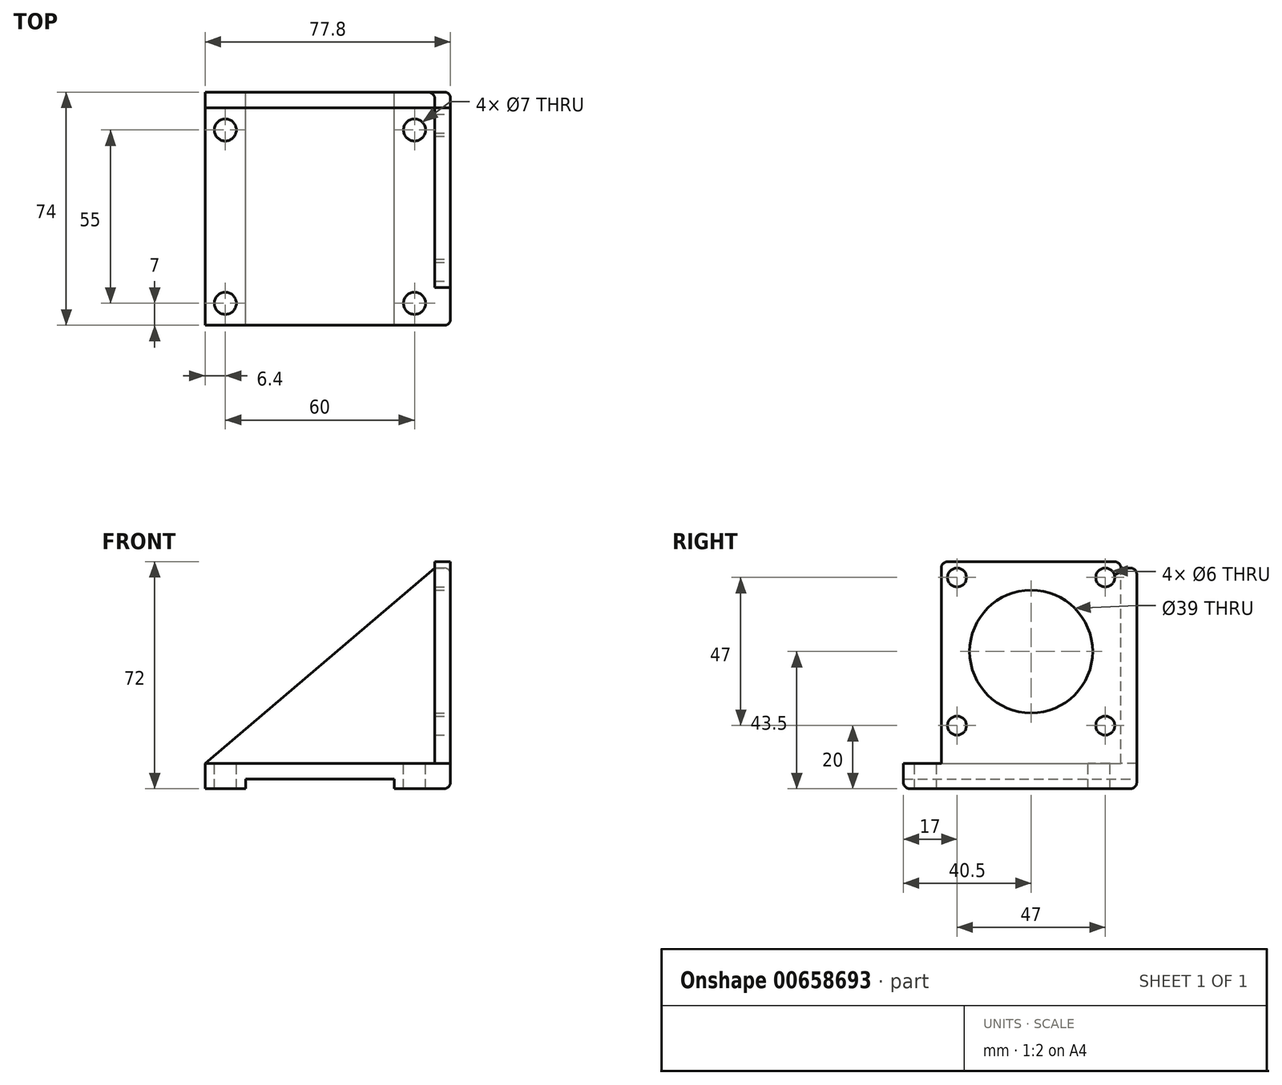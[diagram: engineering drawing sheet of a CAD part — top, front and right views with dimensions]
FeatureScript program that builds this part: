
annotation { "Feature Type Name" : "Feature", "Feature Type Description" : "" }
export const myFeature = defineFeature(function(context is Context, id is Id, definition is map)
    precondition{}
    {
        {
            var Q0;
            Q0=qCreatedBy(makeId("Top.planeOp"),FACE);
            var sketch = newSketch(context, id + "F0", { "sketchPlane" : qUnion([Q0])});
            skLineSegment(sketch, "E0.rect.bottom", {"start": v(36.4, -34.5) * mm, "end": v(-36.4, -34.5) * mm});
            skLineSegment(sketch, "E0.rect.top", {"start": v(36.4, 34.5) * mm, "end": v(-36.4, 34.5) * mm});
            skLineSegment(sketch, "E0.rect.left", {"start": v(36.4, -34.5) * mm, "end": v(36.4, 34.5) * mm});
            skLineSegment(sketch, "E0.rect.right", {"start": v(-36.4, -34.5) * mm, "end": v(-36.4, 34.5) * mm});
            skPoint(sketch, "E0.rect.middle", {"position": v(0, 0) * mm});
            skSolve(sketch);
        }
        {
            var Q0;
            Q0=makeQuery(id+"F0.imprint","IMPRINT",FACE,{"disambiguationData":[TD([[makeQuery(id+"F0.imprint","IMPRINT",EDGE,{"derivedFrom":sQuery(id+"F0.wireOp",EDGE,"E0.rect.bottom")}),-1.0]])]});
            extrude(context, id + "F1", {"entities" : qUnion([Q0]), "depth" : 5 * mm});
        }
        {
            var Q0;
            Q0=makeQuery(id+"F1.opExtrude","CAP_FACE",FACE,{"disambiguationData":[OSD([sQuery(id+"F0.wireOp",EDGE,"E0.rect.bottom"),sQuery(id+"F0.wireOp",EDGE,"E0.rect.top"),sQuery(id+"F0.wireOp",EDGE,"E0.rect.left"),sQuery(id+"F0.wireOp",EDGE,"E0.rect.right")])],"isStart":false});
            var sketch = newSketch(context, id + "F2", { "sketchPlane" : qUnion([Q0])});
            skPoint(sketch, "E1", {"position": v(-30, 27.5) * mm});
            skPoint(sketch, "E2", {"position": v(30, 27.5) * mm});
            skPoint(sketch, "E3", {"position": v(30, -27.5) * mm});
            skPoint(sketch, "E4", {"position": v(-30, -27.5) * mm});
            skLineSegment(sketch, "E5.0", {"start": v(36.4, 34.5) * mm, "end": v(-36.4, 34.5) * mm});
            skLineSegment(sketch, "E6.0", {"start": v(36.4, -34.5) * mm, "end": v(-36.4, -34.5) * mm});
            skSolve(sketch);
        }
        {
            var Q0;
            Q0=sQuery(id+"F2.wireOp",VERTEX,"E1");
            var Q1;
            Q1=sQuery(id+"F2.wireOp",VERTEX,"E2");
            var Q2;
            Q2=sQuery(id+"F2.wireOp",VERTEX,"E3");
            var Q3;
            Q3=sQuery(id+"F2.wireOp",VERTEX,"E4");
            var Q4;
            Q4=makeQuery(id+"F1.opExtrude","SWEPT_BODY",BODY,{"disambiguationData":[OSD([sQuery(id+"F0.wireOp",EDGE,"E0.rect.bottom"),sQuery(id+"F0.wireOp",EDGE,"E0.rect.top"),sQuery(id+"F0.wireOp",EDGE,"E0.rect.left"),sQuery(id+"F0.wireOp",EDGE,"E0.rect.right")])]});
            hole(context, id + "F3", {"style" : HoleStyle.SIMPLE, "holeDiameter" : 7 * mm, "endStyle" : HoleEndStyle.THROUGH, "locations" : qUnion([Q0, Q1, Q2, Q3]), "scope" : qUnion([Q4])});
        }
        {
            var Q0;
            Q0=makeQuery(id+"F1.opExtrude","CAP_FACE",FACE,{"disambiguationData":[OSD([sQuery(id+"F0.wireOp",EDGE,"E0.rect.bottom"),sQuery(id+"F0.wireOp",EDGE,"E0.rect.top"),sQuery(id+"F0.wireOp",EDGE,"E0.rect.left"),sQuery(id+"F0.wireOp",EDGE,"E0.rect.right")])],"isStart":true});
            var sketch = newSketch(context, id + "F4", { "sketchPlane" : qUnion([Q0])});
            skCircle(sketch, "E7.0", {"center": v(-30, 27.5) * mm, "radius": 3.5 * mm});
            skLineSegment(sketch, "E8.bottom", {"start": v(-36.4, 34.5) * mm, "end": v(-23.6, 34.5) * mm});
            skLineSegment(sketch, "E8.top", {"start": v(-36.4, -34.5) * mm, "end": v(-23.6, -34.5) * mm});
            skLineSegment(sketch, "E8.left", {"start": v(-36.4, 34.5) * mm, "end": v(-36.4, -34.5) * mm});
            skLineSegment(sketch, "E8.right", {"start": v(-23.6, 34.5) * mm, "end": v(-23.6, -34.5) * mm});
            skLineSegment(sketch, "E9.bottom", {"start": v(36.4, 34.5) * mm, "end": v(23.6, 34.5) * mm});
            skLineSegment(sketch, "E9.top", {"start": v(36.4, -34.5) * mm, "end": v(23.6, -34.5) * mm});
            skLineSegment(sketch, "E9.left", {"start": v(36.4, 34.5) * mm, "end": v(36.4, -34.5) * mm});
            skLineSegment(sketch, "E9.right", {"start": v(23.6, 34.5) * mm, "end": v(23.6, -34.5) * mm});
            skSolve(sketch);
        }
        {
            var Q0;
            Q0=makeQuery(id+"F4.imprint","IMPRINT",FACE,{"disambiguationData":[TD([[makeQuery(id+"F4.imprint","IMPRINT",EDGE,{"derivedFrom":sQuery(id+"F4.wireOp",EDGE,"E7.0")}),-1.0]])]});
            var Q1;
            Q1=makeQuery(id+"F4.imprint","IMPRINT",FACE,{"disambiguationData":[TD([[makeQuery(id+"F4.imprint","IMPRINT",EDGE,{"derivedFrom":sQuery(id+"F4.wireOp",EDGE,"E9.bottom")}),1.0]])]});
            extrude(context, id + "F5", {"entities" : qUnion([Q0, Q1]), "operationType" : NewBodyOperationType.ADD, "depth" : 3 * mm});
        }
        {
            var Q0;
            Q0=makeQuery(id+"F5.boolean.opBoolean","MERGE",FACE,{"derivedFrom":[makeQuery(id+"F1.opExtrude","SWEPT_FACE",FACE,{"disambiguationData":[OSD([sQuery(id+"F0.wireOp",EDGE,"E0.rect.left")])]}),makeQuery(id+"F5.opExtrude","SWEPT_FACE",FACE,{"disambiguationData":[OSD([sQuery(id+"F4.wireOp",EDGE,"E9.left")])]})]});
            var sketch = newSketch(context, id + "F6", { "sketchPlane" : qUnion([Q0])});
            skLineSegment(sketch, "E10.bottom", {"start": v(34.5, 5) * mm, "end": v(-22.5, 5) * mm});
            skLineSegment(sketch, "E10.top", {"start": v(34.5, 69) * mm, "end": v(-22.5, 69) * mm});
            skLineSegment(sketch, "E10.left", {"start": v(34.5, 5) * mm, "end": v(34.5, 69) * mm});
            skLineSegment(sketch, "E10.right", {"start": v(-22.5, 5) * mm, "end": v(-22.5, 69) * mm});
            skSolve(sketch);
        }
        {
            var Q0;
            Q0=makeQuery(id+"F6.imprint","IMPRINT",FACE,{"disambiguationData":[TD([[makeQuery(id+"F6.imprint","IMPRINT",EDGE,{"derivedFrom":sQuery(id+"F6.wireOp",EDGE,"E10.bottom")}),1.0]])]});
            var Q1;
            {var subQ4=sQuery(id+"F6.wireOp",EDGE,"E10.bottom");Q1=makeQuery(id+"F6.imprint","IMPRINT",FACE,{"disambiguationData":[TD([[makeQuery(id+"F6.imprint","IMPRINT",EDGE,{"derivedFrom":subQ4}),-1.0]])]});}
            extrude(context, id + "F7", {"entities" : qUnion([Q0, Q1]), "operationType" : NewBodyOperationType.ADD, "depth" : 5 * mm});
        }
        {
            var Q0;
            Q0=makeQuery(id+"F7.opExtrude","SWEPT_EDGE",EDGE,{"disambiguationData":[OSD([sQuery(id+"F6.wireOp",EDGE,"E10.top"),sQuery(id+"F6.wireOp",EDGE,"E10.left")])]});
            var Q1;
            Q1=makeQuery(id+"F7.opExtrude","SWEPT_EDGE",EDGE,{"disambiguationData":[OSD([sQuery(id+"F6.wireOp",EDGE,"E10.top"),sQuery(id+"F6.wireOp",EDGE,"E10.right")])]});
            fillet(context, id + "F8", {"entities" : qUnion([Q0, Q1]), "radius" : 2 * mm, "tangentPropagation" : true, "allowEdgeOverflow" : false});
        }
        {
            var Q0;
            Q0=makeQuery(id+"F7.opExtrude","CAP_FACE",FACE,{"disambiguationData":[OSD([sQuery(id+"F0.wireOp",EDGE,"E0.rect.bottom"),sQuery(id+"F0.wireOp",EDGE,"E0.rect.top"),sQuery(id+"F0.wireOp",EDGE,"E0.rect.left"),sQuery(id+"F4.wireOp",EDGE,"E9.bottom"),sQuery(id+"F4.wireOp",EDGE,"E9.top"),sQuery(id+"F4.wireOp",EDGE,"E9.left"),sQuery(id+"F6.wireOp",EDGE,"E10.top"),sQuery(id+"F6.wireOp",EDGE,"E10.left"),sQuery(id+"F6.wireOp",EDGE,"E10.right")])],"isStart":false});
            var sketch = newSketch(context, id + "F9", { "sketchPlane" : qUnion([Q0])});
            skLineSegment(sketch, "E11", {"start": v(6, 69) * mm, "end": v(6, 40.5) * mm, "construction": true});
            skCircle(sketch, "E12", {"center": v(6, 40.5) * mm, "radius": 19.5 * mm});
            skSolve(sketch);
        }
        {
            var Q0;
            Q0=makeQuery(id+"F9.imprint","IMPRINT",FACE,{"disambiguationData":[TD([[makeQuery(id+"F9.imprint","IMPRINT",EDGE,{"derivedFrom":sQuery(id+"F9.wireOp",EDGE,"E12")}),1.0]])]});
            extrude(context, id + "F10", {"entities" : qUnion([Q0]), "operationType" : NewBodyOperationType.REMOVE, "endBound" : BoundingType.THROUGH_ALL, "oppositeDirection" : true, "depth" : 25 * mm});
        }
        {
            var Q0;
            Q0=makeQuery(id+"F7.opExtrude","CAP_FACE",FACE,{"disambiguationData":[OSD([sQuery(id+"F0.wireOp",EDGE,"E0.rect.bottom"),sQuery(id+"F0.wireOp",EDGE,"E0.rect.top"),sQuery(id+"F0.wireOp",EDGE,"E0.rect.left"),sQuery(id+"F4.wireOp",EDGE,"E9.bottom"),sQuery(id+"F4.wireOp",EDGE,"E9.top"),sQuery(id+"F4.wireOp",EDGE,"E9.left"),sQuery(id+"F6.wireOp",EDGE,"E10.top"),sQuery(id+"F6.wireOp",EDGE,"E10.left"),sQuery(id+"F6.wireOp",EDGE,"E10.right")])],"isStart":false});
            var sketch = newSketch(context, id + "F11", { "sketchPlane" : qUnion([Q0])});
            skPoint(sketch, "E13", {"position": v(-17.5, 64) * mm});
            skPoint(sketch, "E14", {"position": v(29.5, 64) * mm});
            skPoint(sketch, "E15", {"position": v(29.5, 17) * mm});
            skPoint(sketch, "E16", {"position": v(-17.5, 17) * mm});
            skCircle(sketch, "E17.0", {"center": v(6, 40.5) * mm, "radius": 19.5 * mm});
            skSolve(sketch);
        }
        {
            var Q0;
            Q0=sQuery(id+"F11.wireOp",VERTEX,"E13");
            var Q1;
            Q1=sQuery(id+"F11.wireOp",VERTEX,"E14");
            var Q2;
            Q2=sQuery(id+"F11.wireOp",VERTEX,"E15");
            var Q3;
            Q3=sQuery(id+"F11.wireOp",VERTEX,"E16");
            var Q4;
            Q4=makeQuery(id+"F1.opExtrude","SWEPT_BODY",BODY,{"disambiguationData":[OSD([sQuery(id+"F0.wireOp",EDGE,"E0.rect.bottom"),sQuery(id+"F0.wireOp",EDGE,"E0.rect.top"),sQuery(id+"F0.wireOp",EDGE,"E0.rect.left"),sQuery(id+"F0.wireOp",EDGE,"E0.rect.right")])]});
            hole(context, id + "F12", {"style" : HoleStyle.SIMPLE, "holeDiameter" : 6 * mm, "endStyle" : HoleEndStyle.THROUGH, "locations" : qUnion([Q0, Q1, Q2, Q3]), "scope" : qUnion([Q4])});
        }
        {
            var Q0;
            {var subQ0=sQuery(id+"F4.wireOp",EDGE,"E9.top");var subQ1=sQuery(id+"F0.wireOp",EDGE,"E0.rect.top");Q0=makeQuery(id+"F7.boolean.opBoolean","MERGE",FACE,{"derivedFrom":[makeQuery(id+"F5.boolean.opBoolean","MERGE",FACE,{"derivedFrom":[makeQuery(id+"F1.opExtrude","SWEPT_FACE",FACE,{"disambiguationData":[OSD([subQ1])]}),makeQuery(id+"F5.opExtrude","SWEPT_FACE",FACE,{"disambiguationData":[OSD([sQuery(id+"F4.wireOp",EDGE,"E8.top")])]}),makeQuery(id+"F5.opExtrude","SWEPT_FACE",FACE,{"disambiguationData":[OSD([subQ0])]})]}),makeQuery(id+"F7.opExtrude","SWEPT_FACE",FACE,{"disambiguationData":[OSD([subQ1,sQuery(id+"F0.wireOp",EDGE,"E0.rect.left"),subQ0,sQuery(id+"F4.wireOp",EDGE,"E9.left"),sQuery(id+"F6.wireOp",EDGE,"E10.left")])]})]});}
            var sketch = newSketch(context, id + "F13", { "sketchPlane" : qUnion([Q0])});
            skLineSegment(sketch, "E18", {"start": v(-36.4, 67) * mm, "end": v(36.4, 5) * mm});
            skSolve(sketch);
        }
        {
            var Q0;
            Q0=makeQuery(id+"F13.imprint","IMPRINT",FACE,{"disambiguationData":[TD([[makeQuery(id+"F13.imprint","IMPRINT",EDGE,{"derivedFrom":sQuery(id+"F13.wireOp",EDGE,"E18")}),-1.0]])]});
            var Q1;
            {var subQ2=sQuery(id+"F0.wireOp",EDGE,"E0.rect.top");Q1=makeQuery(id+"F13.imprint","IMPRINT",FACE,{"disambiguationData":[TD([[makeQuery(id+"F13.imprint","IMPRINT",EDGE,{"derivedFrom":makeQuery(id+"F1.opExtrude","CAP_EDGE",EDGE,{"disambiguationData":[OSD([subQ2])],"isStart":false})}),-1.0]])]});}
            extrude(context, id + "F14", {"entities" : qUnion([Q0, Q1]), "operationType" : NewBodyOperationType.ADD, "depth" : 5 * mm});
        }
        {
            var Q0;
            Q0=makeQuery(id+"F14.opExtrude","CAP_EDGE",EDGE,{"disambiguationData":[OSD([sQuery(id+"F0.wireOp",EDGE,"E0.rect.top"),sQuery(id+"F0.wireOp",EDGE,"E0.rect.left"),sQuery(id+"F4.wireOp",EDGE,"E8.top"),sQuery(id+"F4.wireOp",EDGE,"E9.top"),sQuery(id+"F4.wireOp",EDGE,"E9.left"),sQuery(id+"F6.wireOp",EDGE,"E10.top"),sQuery(id+"F6.wireOp",EDGE,"E10.left")])],"isStart":false});
            fillet(context, id + "F15", {"entities" : qUnion([Q0]), "radius" : 2 * mm, "tangentPropagation" : true, "allowEdgeOverflow" : false});
        }
        {
            var Q0;
            Q0=makeQuery(id+"F14.opExtrude","CAP_EDGE",EDGE,{"disambiguationData":[OSD([sQuery(id+"F0.wireOp",EDGE,"E0.rect.top"),sQuery(id+"F0.wireOp",EDGE,"E0.rect.left"),sQuery(id+"F4.wireOp",EDGE,"E9.top"),sQuery(id+"F4.wireOp",EDGE,"E9.left")])],"isStart":false});
            var Q1;
            Q1=makeQuery(id+"F14.opExtrude","CAP_EDGE",EDGE,{"disambiguationData":[OSD([sQuery(id+"F4.wireOp",EDGE,"E8.top")])],"isStart":false});
            var Q2;
            {var subQ0=sQuery(id+"F4.wireOp",EDGE,"E9.left");var subQ1=sQuery(id+"F4.wireOp",EDGE,"E9.bottom");var subQ2=sQuery(id+"F0.wireOp",EDGE,"E0.rect.left");var subQ3=sQuery(id+"F0.wireOp",EDGE,"E0.rect.bottom");Q2=makeQuery(id+"F7.boolean.opBoolean","MERGE",EDGE,{"derivedFrom":[makeQuery(id+"F5.opExtrude","CAP_EDGE",EDGE,{"disambiguationData":[OSD([subQ1])],"isStart":false}),makeQuery(id+"F7.opExtrude","SWEPT_EDGE",EDGE,{"disambiguationData":[OSD([subQ3,subQ2,subQ1,subQ0]),TDD([makeQuery(id+"F6.imprint","INTERSECT",VERTEX,{"derivedFrom":[makeQuery(id+"F5.opExtrude","CAP_EDGE",EDGE,{"disambiguationData":[OSD([subQ0])],"isStart":false}),makeQuery(id+"F5.boolean.opBoolean","MERGE",EDGE,{"derivedFrom":[makeQuery(id+"F1.opExtrude","SWEPT_EDGE",EDGE,{"disambiguationData":[OSD([subQ3,subQ2])]}),makeQuery(id+"F5.opExtrude","SWEPT_EDGE",EDGE,{"disambiguationData":[OSD([subQ1,subQ0])]})]})]})])]})]});}
            var Q3;
            Q3=makeQuery(id+"F5.opExtrude","CAP_EDGE",EDGE,{"disambiguationData":[OSD([sQuery(id+"F4.wireOp",EDGE,"E8.bottom")])],"isStart":false});
            var Q4;
            Q4=makeQuery(id+"F7.opExtrude","CAP_EDGE",EDGE,{"disambiguationData":[OSD([sQuery(id+"F0.wireOp",EDGE,"E0.rect.bottom"),sQuery(id+"F0.wireOp",EDGE,"E0.rect.left"),sQuery(id+"F4.wireOp",EDGE,"E9.bottom"),sQuery(id+"F4.wireOp",EDGE,"E9.left")])],"isStart":false});
            fillet(context, id + "F16", {"entities" : qUnion([Q0, Q1, Q2, Q3, Q4]), "radius" : 2 * mm, "tangentPropagation" : true, "allowEdgeOverflow" : false});
        }
        {
            var Q0;
            {var subQ0=sQuery(id+"F4.wireOp",EDGE,"E9.left");Q0=makeQuery(id+"F14.boolean.opBoolean","MERGE",EDGE,{"derivedFrom":[makeQuery(id+"F7.opExtrude","CAP_EDGE",EDGE,{"disambiguationData":[OSD([subQ0])],"isStart":false}),makeQuery(id+"F14.opExtrude","SWEPT_EDGE",EDGE,{"disambiguationData":[OSD([sQuery(id+"F0.wireOp",EDGE,"E0.rect.top"),sQuery(id+"F0.wireOp",EDGE,"E0.rect.left"),sQuery(id+"F4.wireOp",EDGE,"E9.top"),subQ0,sQuery(id+"F6.wireOp",EDGE,"E10.left")])]})]});}
            fillet(context, id + "F17", {"entities" : qUnion([Q0]), "radius" : 2 * mm, "tangentPropagation" : true, "allowEdgeOverflow" : false});
        }
    });
